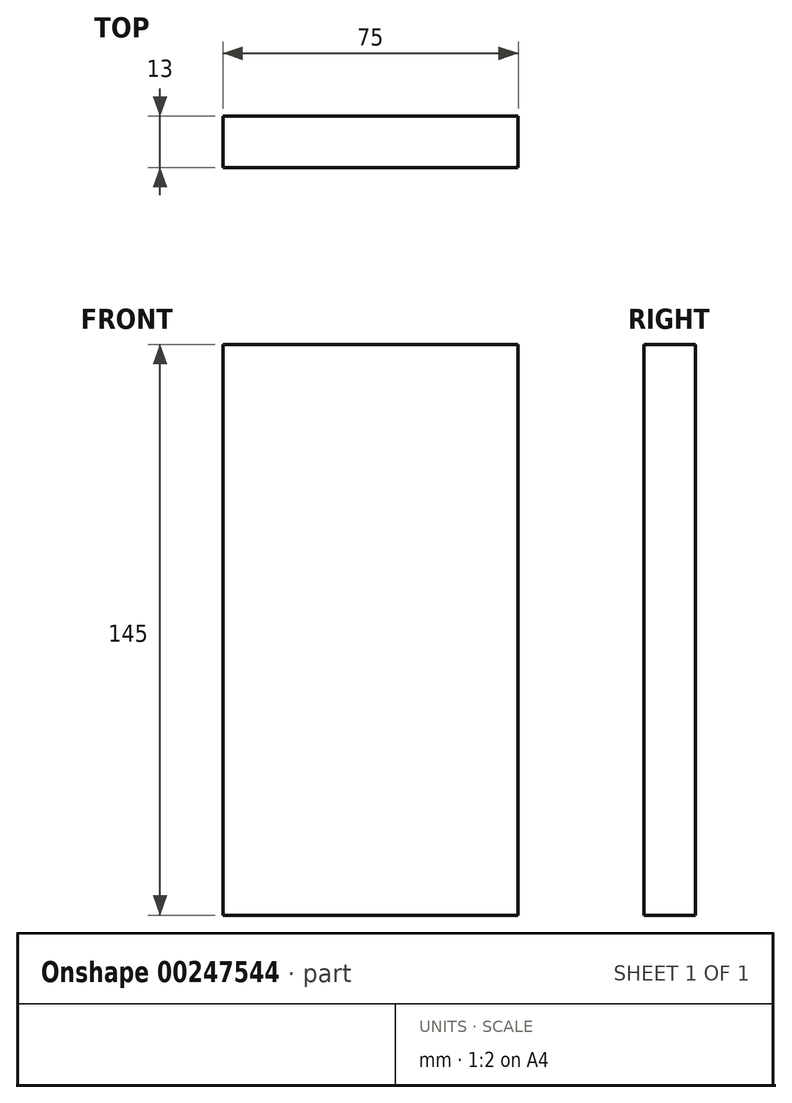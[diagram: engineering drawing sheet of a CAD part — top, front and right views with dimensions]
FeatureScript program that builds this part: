
annotation { "Feature Type Name" : "Feature", "Feature Type Description" : "" }
export const myFeature = defineFeature(function(context is Context, id is Id, definition is map)
    precondition{}
    {
        {
            var Q0;
            Q0=qCreatedBy(makeId("Front.planeOp"),FACE);
            var sketch = newSketch(context, id + "F0", { "sketchPlane" : qUnion([Q0])});
            skLineSegment(sketch, "E0.bottom", {"start": v(-45.88, 69.98) * mm, "end": v(29.12, 69.98) * mm});
            skLineSegment(sketch, "E0.top", {"start": v(-45.88, -75.02) * mm, "end": v(29.12, -75.02) * mm});
            skLineSegment(sketch, "E0.left", {"start": v(-45.88, 69.98) * mm, "end": v(-45.88, -75.02) * mm});
            skLineSegment(sketch, "E0.right", {"start": v(29.12, 69.98) * mm, "end": v(29.12, -75.02) * mm});
            skSolve(sketch);
        }
        {
            var Q0;
            Q0=makeQuery(id+"F0.imprint","IMPRINT",FACE,{"disambiguationData":[TD([[makeQuery(id+"F0.imprint","IMPRINT",EDGE,{"derivedFrom":sQuery(id+"F0.wireOp",EDGE,"E0.bottom")}),-1.0]])]});
            extrude(context, id + "F1", {"entities" : qUnion([Q0]), "endBound" : BoundingType.SYMMETRIC, "depth" : 13 * mm});
        }
    });
